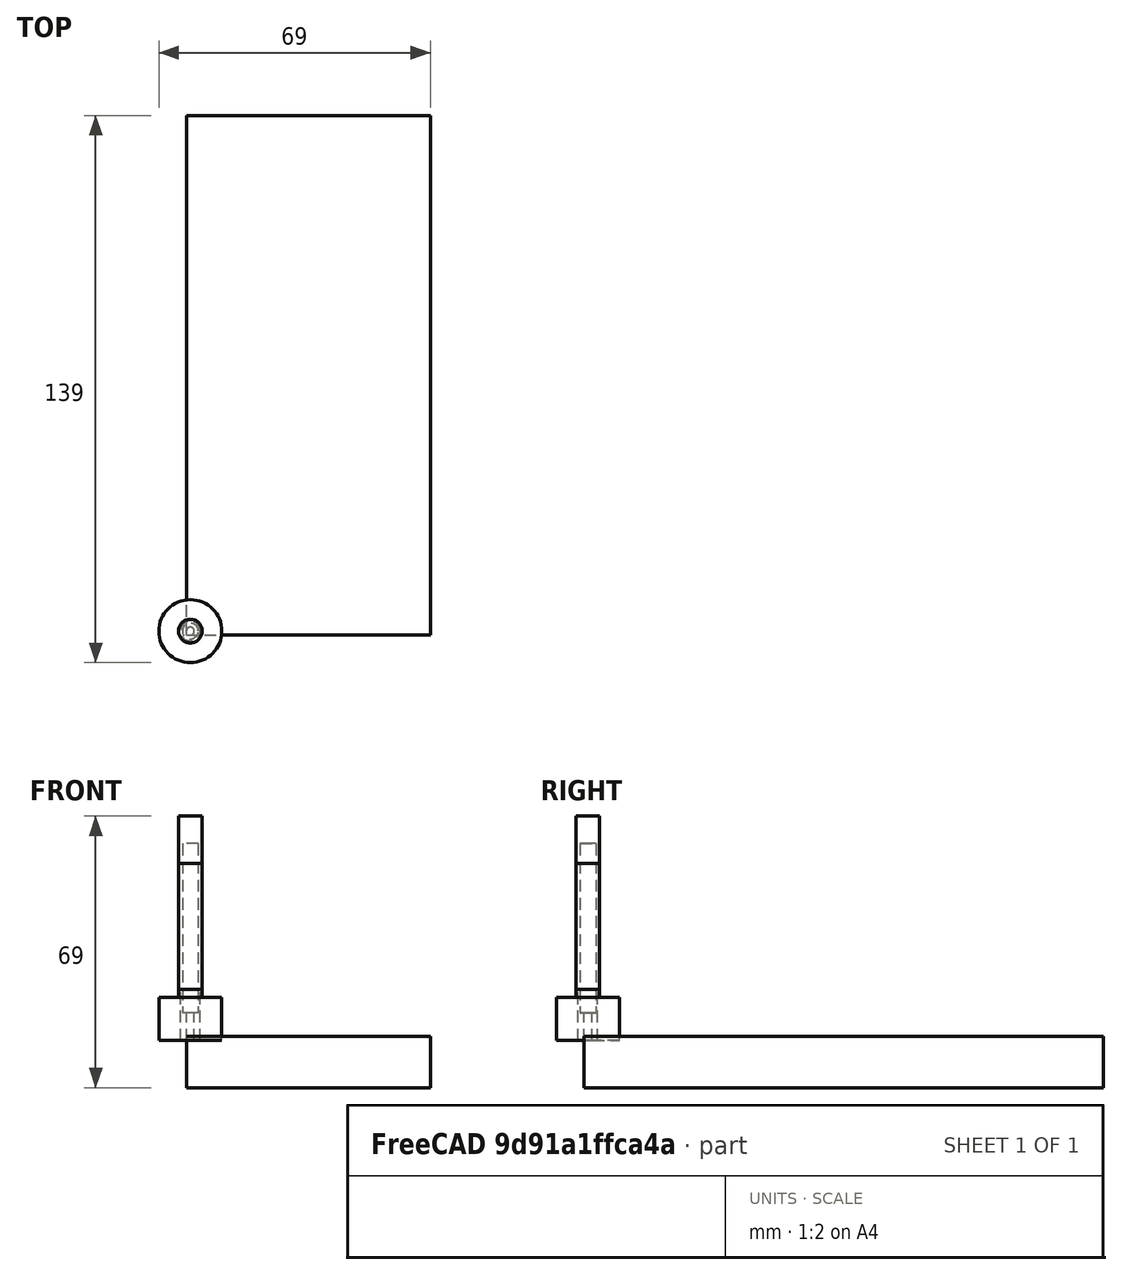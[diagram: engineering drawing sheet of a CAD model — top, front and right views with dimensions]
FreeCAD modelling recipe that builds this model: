
FCSTD DOCUMENT  (FreeCAD 0.21R33771 (Git))
Label: kumiko_strips
License: All rights reserved
LicenseURL: http://en.wikipedia.org/wiki/All_rights_reserved
objects: Path::FeaturePython×9, Part::FeaturePython×5, App::DocumentObjectGroup×3, Sketcher::SketchObject×1, App::Link×1, PartDesign::Pad×1, PartDesign::Body×1, App::FeaturePython×1, Mesh::FeaturePython×1
note: 14 computed .brp shape members not serialized (recipe doc carries the construction recipe); baked Part::Feature solids carry a one-line shape summary decoded from their .brp
EXTERNAL_REF file=../master_kumiko_box.FCStd obj=Spreadsheet

FEATURE [Sketcher::SketchObject] Sketch
  FullyConstrained = true
  MapMode = 5
  Placement = pos=(0,0,0) rot=(0.57735,0.57735,0.57735;2.0944rad)
  Support = -> [YZ_Plane]
  expr: Constraints[13] = <<SpreadSheet>>.lid_frame_width
  expr: Constraints[14] = <<SpreadSheet>>.kumiko_hight / 2
  expr: Constraints[15] = <<SpreadSheet>>.kumiko_thickness
  expr: Constraints[27] = <<SpreadSheet>>.kumiko_grid_size
  expr: Constraints[6] = <<SpreadSheet>>.box_length
  expr: Constraints[7] = <<SpreadSheet>>.kumiko_hight
  sketch-geometry (24):
    g0: LineSegment StartX=0 StartY=0 StartZ=0 EndX=130 EndY=0 EndZ=0
    g1: LineSegment StartX=130 StartY=0 StartZ=0 EndX=130 EndY=11 EndZ=0
    g2: LineSegment StartX=0 StartY=11 StartZ=0 EndX=0 EndY=0 EndZ=0
    g3: LineSegment StartX=11.5 StartY=11 StartZ=0 EndX=11.5 EndY=5.5 EndZ=0
    g4: LineSegment StartX=11.5 StartY=5.5 StartZ=0 EndX=8.5 EndY=5.5 EndZ=0
    g5: LineSegment StartX=8.5 StartY=5.5 StartZ=0 EndX=8.5 EndY=11 EndZ=0
    g6: LineSegment StartX=39 StartY=11 StartZ=0 EndX=39 EndY=5.5 EndZ=0
    g7: LineSegment StartX=39 StartY=5.5 StartZ=0 EndX=36 EndY=5.5 EndZ=0
    g8: LineSegment StartX=36 StartY=5.5 StartZ=0 EndX=36 EndY=11 EndZ=0
    g9: LineSegment StartX=0 StartY=11 StartZ=0 EndX=8.5 EndY=11 EndZ=0
    g10: LineSegment StartX=11.5 StartY=11 StartZ=0 EndX=36 EndY=11 EndZ=0
    g11: LineSegment StartX=39 StartY=11 StartZ=0 EndX=63.5 EndY=11 EndZ=0
    g12: LineSegment StartX=66.5 StartY=11 StartZ=0 EndX=66.5 EndY=5.5 EndZ=0
    g13: LineSegment StartX=66.5 StartY=5.5 StartZ=0 EndX=63.5 EndY=5.5 EndZ=0
    g14: LineSegment StartX=63.5 StartY=5.5 StartZ=0 EndX=63.5 EndY=11 EndZ=0
    g15: LineSegment StartX=66.5 StartY=11 StartZ=0 EndX=91 EndY=11 EndZ=0
    g16: LineSegment StartX=91 StartY=11 StartZ=0 EndX=91 EndY=5.5 EndZ=0
    g17: LineSegment StartX=91 StartY=5.5 StartZ=0 EndX=94 EndY=5.5 EndZ=0
    g18: LineSegment StartX=94 StartY=5.5 StartZ=0 EndX=94 EndY=11 EndZ=0
    g19: LineSegment StartX=94 StartY=11 StartZ=0 EndX=118.5 EndY=11 EndZ=0
    g20: LineSegment StartX=118.5 StartY=11 StartZ=0 EndX=118.5 EndY=5.5 EndZ=0
    g21: LineSegment StartX=118.5 StartY=5.5 StartZ=0 EndX=121.5 EndY=5.5 EndZ=0
    g22: LineSegment StartX=121.5 StartY=5.5 StartZ=0 EndX=121.5 EndY=11 EndZ=0
    g23: LineSegment StartX=121.5 StartY=11 StartZ=0 EndX=130 EndY=11 EndZ=0
  constraints (71):
    c: Coincident(g0,g1)
    c: Coincident(g2,g0)
    c: Horizontal(g0)
    c: Vertical(g1)
    c: Vertical(g2)
    c: Coincident(g0,g-1)
    c: DistanceX(g0,g0) = 130
    c: DistanceY(g2,g2) = 11
    c: Coincident(g3,g4)
    c: Coincident(g4,g5)
    c: Horizontal(g4)
    c: Vertical(g3)
    c: Vertical(g5)
    c: DistanceX(g2,g5) = 8.5
    c: DistanceY(g3,g3) = 5.5
    c: DistanceX(g4,g4) = 3
    c: Coincident(g6,g7)
    c: Coincident(g7,g8)
    c: Horizontal(g7)
    c: Vertical(g6)
    c: Vertical(g8)
    c: Coincident(g9,g2)
    c: Coincident(g9,g5)
    c: Horizontal(g9)
    c: Equal(g5,g3)
    c: Equal(g4,g7)
    c: Equal(g5,g8)
    c: DistanceX(g5,g8) = 27.5
    c: Equal(g6,g8)
    c: Equal(g2,g1)
    c: Coincident(g10,g3)
    c: Coincident(g10,g8)
    c: Horizontal(g10)
    c: Coincident(g11,g6)
    c: Horizontal(g11)
    c: Equal(g10,g11)
    c: Coincident(g12,g13)
    c: Coincident(g13,g14)
    c: Horizontal(g13)
    c: Vertical(g12)
    c: Vertical(g14)
    c: Equal(g6,g14)
    c: Equal(g13,g7)
    c: Coincident(g14,g11)
    c: Equal(g14,g12)
    c: Coincident(g15,g12)
    c: Horizontal(g15)
    c: Coincident(g16,g15)
    c: Vertical(g16)
    c: Coincident(g17,g16)
    c: Horizontal(g17)
    c: Coincident(g18,g17)
    c: Vertical(g18)
    c: Equal(g16,g18)
    c: Equal(g16,g12)
    c: Equal(g13,g17)
    c: Equal(g15,g11)
    c: Coincident(g19,g18)
    c: Horizontal(g19)
    c: Coincident(g20,g19)
    c: Vertical(g20)
    c: Coincident(g21,g20)
    c: Horizontal(g21)
    c: Coincident(g22,g21)
    c: Vertical(g22)
    c: Coincident(g23,g22)
    c: Coincident(g23,g1)
    c: Horizontal(g23)
    c: Equal(g15,g19)
    c: Equal(g17,g21)
    c: Equal(g18,g20)
FEATURE [App::Link] Link  label="SpreadSheet"
  LinkedObject = -> <external ../master_kumiko_box.FCStd>#Spreadsheet
FEATURE [PartDesign::Pad] Pad
  Direction = (1,-2e-16,3e-16)
  Length = 60
  Length2 = 10
  Placement = pos=(0,0,0) rot=(0.57735,0.57735,0.57735;2.0944rad)
  Profile = -> Sketch
  ReferenceAxis = -> Sketch [N_Axis]
  Type = 0
  expr: Length = <<SpreadSheet>>.kumiko_thickness * 2 * 10
FEATURE [PartDesign::Body] Body
  Group = -> [Sketch,Pad]
  Origin = -> Origin
  Placement = pos=(0,0,-11) rot=(0,0,1;0rad)
  Tip = -> Pad
  expr: .Placement.Base.z = -<<SpreadSheet>>.kumiko_hight
FEATURE [App::FeaturePython] SetupSheet  # Path/CAM operation (typed FeaturePython)
  ClearanceHeightExpression = OpStockZMax+SetupSheet.ClearanceHeightOffset
  ClearanceHeightOffset = 5
  CoolantMode = 0
  CoolantModes = None | Flood | Mist
  FinalDepthExpression = OpFinalDepth
  HorizRapid = 0
  SafeHeightExpression = OpStockZMax+SetupSheet.SafeHeightOffset
  SafeHeightOffset = 3
  StartDepthExpression = OpStartDepth
  StepDownExpression = OpToolDiameter
  VertRapid = 0
FEATURE [Part::FeaturePython] Clone  label="Model-Body"  # Draft clone (typed FeaturePython)
  AttacherType = Attacher::AttachEngine3D
  Fuse = false
  Objects = -> [Body]
  PathResource = Model
  Placement = pos=(0,0,-11) rot=(0,0,1;0rad)
  Scale = (1,1,1)
FEATURE [App::DocumentObjectGroup] Model
  Group = -> [Clone]
FEATURE [Part::FeaturePython] Stock  # WARN: FeaturePython — macro-defined, semantics opaque (R4)
  Base = -> Model
  ExtXneg = 1
  ExtXpos = 1
  ExtYneg = 1
  ExtYpos = 1
  ExtZneg = 1
  ExtZpos = 1
  Placement = pos=(-6e-15,-3.3e-14,-11) rot=(0,0,1;0rad)
  StockType = FromBase
FEATURE [Part::FeaturePython] ToolBit001  label="FREES_VLAK_16_mm"  # Path/CAM toolbit (typed FeaturePython)
  BitPropertyNames = Chipload | CuttingEdgeHeight | Diameter | Flutes | Length | Material | ShankDiameter | SpindleDirection
  BitShape = /Applications/FreeCAD.app/Contents/Resources/Mod/Path/Tools/Shape/endmill.fcstd
  Chipload = 0
  CuttingEdgeHeight = 11
  Diameter = 16
  File = <userpath>/Library/Application Support/FreeCAD/Macro/FREES_VLAK_16_mm.fctb
  Flutes = 0
  Length = 45
  Material = 0
  ShankDiameter = 6
  ShapeName = endmill
  SpindleDirection = 0
FEATURE [Path::FeaturePython] FREES_VLAK_16_mm  label="FREES_VLAK_16_mm001"  # Path/CAM operation (typed FeaturePython)
  HorizFeed = 0
  HorizRapid = 0
  SpindleDir = 0
  SpindleSpeed = 0
  Tool = -> ToolBit001
  ToolNumber = 2
  VertFeed = 0
  VertRapid = 0
  expr: HorizRapid = SetupSheet.HorizRapid
  expr: VertRapid = SetupSheet.VertRapid
FEATURE [Part::FeaturePython] ToolBit002  label="FREES_5mm"  # Path/CAM toolbit (typed FeaturePython)
  BitPropertyNames = Chipload | CuttingEdgeHeight | Diameter | Flutes | Length | Material | ShankDiameter | SpindleDirection
  BitShape = /Applications/FreeCAD.app/Contents/Resources/Mod/Path/Tools/Shape/endmill.fcstd
  Chipload = 0
  CuttingEdgeHeight = 13
  Diameter = 5
  File = <userpath>/Library/Application Support/FreeCAD/Macro/FREES_5mm.fctb
  Flutes = 0
  Length = 57
  Material = 0
  ShankDiameter = 6
  ShapeName = endmill
  SpindleDirection = 0
FEATURE [Path::FeaturePython] FREES_5mm  label="FREES_5mm001"  # Path/CAM operation (typed FeaturePython)
  HorizFeed = 0
  HorizRapid = 0
  SpindleDir = 0
  SpindleSpeed = 0
  Tool = -> ToolBit002
  ToolNumber = 3
  VertFeed = 0
  VertRapid = 0
  expr: HorizRapid = SetupSheet.HorizRapid
  expr: VertRapid = SetupSheet.VertRapid
FEATURE [Part::FeaturePython] ToolBit003  label="FREES_2_mm"  # Path/CAM toolbit (typed FeaturePython)
  BitPropertyNames = Chipload | CuttingEdgeHeight | Diameter | Flutes | Length | Material | ShankDiameter | SpindleDirection
  BitShape = /Applications/FreeCAD.app/Contents/Resources/Mod/Path/Tools/Shape/endmill.fcstd
  Chipload = 0
  CuttingEdgeHeight = 7
  Diameter = 2
  File = <userpath>/Library/Application Support/FreeCAD/Macro/FREES_2_mm.fctb
  Flutes = 0
  Length = 50
  Material = 0
  ShankDiameter = 4
  ShapeName = endmill
  SpindleDirection = 0
FEATURE [Path::FeaturePython] FREES_2_mm  label="FREES_2_mm001"  # Path/CAM operation (typed FeaturePython)
  HorizFeed = 0
  HorizRapid = 0
  SpindleDir = 0
  SpindleSpeed = 0
  Tool = -> ToolBit003
  ToolNumber = 4
  VertFeed = 0
  VertRapid = 0
  expr: HorizRapid = SetupSheet.HorizRapid
  expr: VertRapid = SetupSheet.VertRapid
FEATURE [App::DocumentObjectGroup] Tools
  Group = -> [FREES_VLAK_16_mm,FREES_5mm,FREES_2_mm]
FEATURE [Path::FeaturePython] MillFace  # Path/CAM operation (typed FeaturePython)
  Active = true
  AreaParams:
    Tolerance = 1e-07
    FitArcs = True
    Simplify = False
    CleanDistance = 0.0
    Accuracy = 0.01
    Unit = 1.0
    MinArcPoints = 4
    MaxArcPoints = 100
    ClipperScale = 10000000.0
    Fill = 0
    Coplanar = 0
    Reorient = True
    Outline = False
    Explode = False
    OpenMode = 0
    Deflection = 0.01
    SubjectFill = 0
    ClipFill = 0
    Offset = 0.0
    ExtraPass = 0
    Stepover = 0.0
    LastStepover = 0.0
    JoinType = 0
    EndType = 0
    MiterLimit = 2.0
    RoundPrecision = 0.0
    PocketMode = 1
    ToolRadius = 8.0
    PocketExtraOffset = 0.0
    PocketStepover = 8.0
    PocketLastStepover = 0.0
    FromCenter = True
    Angle = 45.0
    AngleShift = 0.0
    Shift = 0.0
    Thicken = False
    SectionCount = -1
    Stepdown = 1.0
    SectionOffset = 0.0
    SectionTolerance = 1e-07
    SectionMode = 2
    Project = False
  Base = -> [Clone]
  BoundaryShape = 0
  ClearEdges = true
  ClearanceHeight = 6
  CoolantMode = 0
  CutMode = 0
  CycleTime = Cycletime Error
  ExcludeRaisedAreas = false
  ExtraOffset = 0
  FinalDepth = 2.49e-14
  FinishDepth = 0.5
  KeepToolDown = false
  MinTravel = false
  OffsetPattern = 0
  OpFinalDepth = 2.49e-14
  OpStartDepth = 1
  OpStockZMax = 1
  OpStockZMin = -12
  OpToolDiameter = 16
  PathParams = {'orientation': 1, 'feedrate': 0.0, 'feedrate_v': 0.0, 'verbose': True, 'resume_height': 4.000000000000028, 'retraction': 6.000000000000028, 'return_end': True, 'preamble': False, 'start': Vector (0.0, 0.0, 0.0)}
  PocketLastStepOver = 0
  SafeHeight = 4
  SplitArcs = false
  StartAt = 0
  StartDepth = 1
  StartPoint = (0,0,0)
  StepDown = 1
  StepOver = 50
  ToolController = -> FREES_VLAK_16_mm
  UseStartPoint = true
  ZigZagAngle = 45
  expr: ClearanceHeight = OpStockZMax + SetupSheet.ClearanceHeightOffset
  expr: FinalDepth = OpFinalDepth
  expr: FinishDepth = 0.5 mm
  expr: SafeHeight = OpStockZMax + SetupSheet.SafeHeightOffset
  expr: StartDepth = OpStartDepth
  expr: StepDown = 1
FEATURE [Path::FeaturePython] Profile  # Path/CAM operation (typed FeaturePython)
  Active = true
  AreaParams:
    Tolerance = 1e-07
    FitArcs = True
    Simplify = False
    CleanDistance = 0.0
    Accuracy = 0.01
    Unit = 1.0
    MinArcPoints = 4
    MaxArcPoints = 100
    ClipperScale = 10000000.0
    Fill = 0
    Coplanar = 0
    Reorient = True
    Outline = False
    Explode = False
    OpenMode = 0
    Deflection = 0.01
    SubjectFill = 0
    ClipFill = 0
    Offset = 2.5
    ExtraPass = 0
    Stepover = 0.0
    LastStepover = 0.0
    JoinType = 0
    EndType = 0
    MiterLimit = 2.0
    RoundPrecision = 0.0
    PocketMode = 0
    ToolRadius = 1.0
    PocketExtraOffset = 0.0
    PocketStepover = 0.0
    PocketLastStepover = 0.0
    FromCenter = False
    Angle = 45.0
    AngleShift = 0.0
    Shift = 0.0
    Thicken = False
    SectionCount = -1
    Stepdown = 1.0
    SectionOffset = 0.0
    SectionTolerance = 1e-07
    SectionMode = 2
    Project = False
  Base = -> [Clone]
  ClearanceHeight = 6
  CoolantMode = 0
  CycleTime = Cycletime Error
  Direction = 0
  FinalDepth = -11
  HandleMultipleFeatures = 0
  JoinType = 0
  MiterLimit = 0.1
  OffsetExtra = 0
  OpFinalDepth = -11
  OpStartDepth = 1
  OpStockZMax = 1
  OpStockZMin = -12
  OpToolDiameter = 5
  PathParams = {'orientation': 1, 'feedrate': 0.0, 'feedrate_v': 0.0, 'verbose': True, 'resume_height': 4.000000000000028, 'retraction': 6.000000000000028, 'return_end': True, 'preamble': False, 'start': Vector (0.0, 0.0, 0.0)}
  SafeHeight = 4
  Side = 0
  SplitArcs = false
  StartDepth = 1
  StartPoint = (0,0,0)
  StepDown = 2.5
  ToolController = -> FREES_5mm
  UseComp = true
  UseStartPoint = true
  processCircles = false
  processHoles = false
  processPerimeter = true
  expr: ClearanceHeight = OpStockZMax + SetupSheet.ClearanceHeightOffset
  expr: FinalDepth = OpFinalDepth
  expr: SafeHeight = OpStockZMax + SetupSheet.SafeHeightOffset
  expr: StartDepth = OpStartDepth
  expr: StepDown = 2.5
FEATURE [Path::FeaturePython] Pocket_Shape  # Path/CAM operation (typed FeaturePython)
  Active = true
  AreaParams:
    Tolerance = 1e-07
    FitArcs = True
    Simplify = False
    CleanDistance = 0.0
    Accuracy = 0.01
    Unit = 1.0
    MinArcPoints = 4
    MaxArcPoints = 100
    ClipperScale = 10000000.0
    Fill = 0
    Coplanar = 0
    Reorient = True
    Outline = False
    Explode = False
    OpenMode = 0
    Deflection = 0.01
    SubjectFill = 0
    ClipFill = 0
    Offset = 0.0
    ExtraPass = 0
    Stepover = 0.0
    LastStepover = 0.0
    JoinType = 0
    EndType = 0
    MiterLimit = 2.0
    RoundPrecision = 0.0
    PocketMode = 1
    ToolRadius = 1.0
    PocketExtraOffset = 0.0
    PocketStepover = 1.6
    PocketLastStepover = 0.0
    FromCenter = True
    Angle = 90.0
    AngleShift = 0.0
    Shift = 0.0
    Thicken = False
    SectionCount = -1
    Stepdown = 1.0
    SectionOffset = 0.0
    SectionTolerance = 1e-07
    SectionMode = 2
    Project = False
  Base = -> [Clone]
  ClearanceHeight = 6
  CoolantMode = 0
  CutMode = 0
  CycleTime = Cycletime Error
  ExtensionCorners = true
  ExtensionFeature = -> [Clone]
  ExtensionLengthDefault = 1
  ExtraOffset = 0
  FinalDepth = -5.5
  FinishDepth = 0.5
  KeepToolDown = false
  MinTravel = false
  OffsetPattern = 0
  OpFinalDepth = -5.5
  OpStartDepth = 1
  OpStockZMax = 1
  OpStockZMin = -12
  OpToolDiameter = 2
  PathParams = {'orientation': 1, 'feedrate': 0.0, 'feedrate_v': 0.0, 'verbose': True, 'resume_height': 4.000000000000028, 'retraction': 6.000000000000028, 'return_end': True, 'preamble': False}
  PocketLastStepOver = 0
  SafeHeight = 4
  SplitArcs = false
  StartAt = 0
  StartDepth = 1
  StartPoint = (0,0,0)
  StepDown = 1.5
  StepOver = 80
  ToolController = -> FREES_2_mm
  UseOutline = false
  UseStartPoint = false
  ZigZagAngle = 90
  expr: ClearanceHeight = OpStockZMax + SetupSheet.ClearanceHeightOffset
  expr: ExtensionLengthDefault = OpToolDiameter / 2
  expr: FinalDepth = OpFinalDepth
  expr: SafeHeight = OpStockZMax + SetupSheet.SafeHeightOffset
  expr: StartDepth = OpStartDepth
  expr: StepDown = 1.5
FEATURE [Path::FeaturePython] Pocket_Shape001  # Path/CAM operation (typed FeaturePython)
  Active = true
  AreaParams:
    Tolerance = 1e-07
    FitArcs = True
    Simplify = False
    CleanDistance = 0.0
    Accuracy = 0.01
    Unit = 1.0
    MinArcPoints = 4
    MaxArcPoints = 100
    ClipperScale = 10000000.0
    Fill = 0
    Coplanar = 0
    Reorient = True
    Outline = False
    Explode = False
    OpenMode = 0
    Deflection = 0.01
    SubjectFill = 0
    ClipFill = 0
    Offset = 0.0
    ExtraPass = 0
    Stepover = 0.0
    LastStepover = 0.0
    JoinType = 0
    EndType = 0
    MiterLimit = 2.0
    RoundPrecision = 0.0
    PocketMode = 1
    ToolRadius = 1.0
    PocketExtraOffset = 0.0
    PocketStepover = 1.6
    PocketLastStepover = 0.0
    FromCenter = True
    Angle = 0.0
    AngleShift = 0.0
    Shift = 0.0
    Thicken = False
    SectionCount = -1
    Stepdown = 1.0
    SectionOffset = 0.0
    SectionTolerance = 1e-07
    SectionMode = 2
    Project = False
  Base = -> [Clone]
  ClearanceHeight = 6
  CoolantMode = 0
  CutMode = 0
  CycleTime = Cycletime Error
  ExtensionCorners = true
  ExtensionFeature = -> [Clone]
  ExtensionLengthDefault = 1
  ExtraOffset = 0
  FinalDepth = -5.5
  FinishDepth = 0.5
  KeepToolDown = false
  MinTravel = false
  OffsetPattern = 0
  OpFinalDepth = -5.5
  OpStartDepth = 1
  OpStockZMax = 1
  OpStockZMin = -12
  OpToolDiameter = 2
  PathParams = {'orientation': 1, 'feedrate': 0.0, 'feedrate_v': 0.0, 'verbose': True, 'resume_height': 4.000000000000028, 'retraction': 6.000000000000028, 'return_end': True, 'preamble': False, 'start': Vector (59.99999999999996, 92.00000000000357, 6.000000000000028)}
  PocketLastStepOver = 0
  SafeHeight = 4
  SplitArcs = false
  StartAt = 0
  StartDepth = 1
  StartPoint = (0,0,0)
  StepDown = 1.5
  StepOver = 80
  ToolController = -> FREES_2_mm
  UseOutline = false
  UseStartPoint = false
  ZigZagAngle = 0
  expr: ClearanceHeight = OpStockZMax + SetupSheet.ClearanceHeightOffset
  expr: ExtensionLengthDefault = OpToolDiameter / 2
  expr: FinalDepth = OpFinalDepth
  expr: SafeHeight = OpStockZMax + SetupSheet.SafeHeightOffset
  expr: StartDepth = OpStartDepth
  expr: StepDown = 1.5
FEATURE [Path::FeaturePython] Pocket_Shape002  # Path/CAM operation (typed FeaturePython)
  Active = true
  AreaParams:
    Tolerance = 1e-07
    FitArcs = True
    Simplify = False
    CleanDistance = 0.0
    Accuracy = 0.01
    Unit = 1.0
    MinArcPoints = 4
    MaxArcPoints = 100
    ClipperScale = 10000000.0
    Fill = 0
    Coplanar = 0
    Reorient = True
    Outline = False
    Explode = False
    OpenMode = 0
    Deflection = 0.01
    SubjectFill = 0
    ClipFill = 0
    Offset = 0.0
    ExtraPass = 0
    Stepover = 0.0
    LastStepover = 0.0
    JoinType = 0
    EndType = 0
    MiterLimit = 2.0
    RoundPrecision = 0.0
    PocketMode = 1
    ToolRadius = 1.0
    PocketExtraOffset = 0.0
    PocketStepover = 1.6
    PocketLastStepover = 0.0
    FromCenter = True
    Angle = 0.0
    AngleShift = 0.0
    Shift = 0.0
    Thicken = False
    SectionCount = -1
    Stepdown = 1.0
    SectionOffset = 0.0
    SectionTolerance = 1e-07
    SectionMode = 2
    Project = False
  Base = -> [Clone]
  ClearanceHeight = 6
  CoolantMode = 0
  CutMode = 0
  CycleTime = Cycletime Error
  ExtensionCorners = true
  ExtensionFeature = -> [Clone]
  ExtensionLengthDefault = 1
  ExtraOffset = 0
  FinalDepth = -5.5
  FinishDepth = 0.5
  KeepToolDown = false
  MinTravel = false
  OffsetPattern = 0
  OpFinalDepth = -5.5
  OpStartDepth = 1
  OpStockZMax = 1
  OpStockZMin = -12
  OpToolDiameter = 2
  PathParams = {'orientation': 1, 'feedrate': 0.0, 'feedrate_v': 0.0, 'verbose': True, 'resume_height': 4.000000000000028, 'retraction': 6.000000000000028, 'return_end': True, 'preamble': False}
  PocketLastStepOver = 0
  SafeHeight = 4
  SplitArcs = false
  StartAt = 0
  StartDepth = 1
  StartPoint = (0,0,0)
  StepDown = 1.5
  StepOver = 80
  ToolController = -> FREES_2_mm
  UseOutline = false
  UseStartPoint = false
  ZigZagAngle = 0
  expr: ClearanceHeight = OpStockZMax + SetupSheet.ClearanceHeightOffset
  expr: ExtensionLengthDefault = OpToolDiameter / 2
  expr: FinalDepth = OpFinalDepth
  expr: SafeHeight = OpStockZMax + SetupSheet.SafeHeightOffset
  expr: StartDepth = OpStartDepth
  expr: StepDown = 1.5
FEATURE [App::DocumentObjectGroup] Operations
  Group = -> [MillFace,Profile,Pocket_Shape,Pocket_Shape001,Pocket_Shape002]
FEATURE [Path::FeaturePython] Job  # Path/CAM operation (typed FeaturePython)
  CycleTime = 00:00:00
  Fixtures = G54
  GeometryTolerance = 0.01
  JobType = 0
  LastPostProcessDate = 2024-04-25 20:54:02.900377
  LastPostProcessOutput = <userpath>/Documents/jewelry_kumiko_box/cnc/bin/kumiko_strips.nc
  Model = -> Model
  Operations = -> Operations
  OrderOutputBy = 0
  PostProcessor = 14
  PostProcessorOutputFile = <userpath>/Documents/jewelry_kumiko_box/cnc/bin/kumiko_strips
  SetupSheet = -> SetupSheet
  SplitOutput = false
  Stock = -> Stock
  Tools = -> Tools
FEATURE [Mesh::FeaturePython] CutMaterial  # WARN: FeaturePython — macro-defined, semantics opaque (R4)
